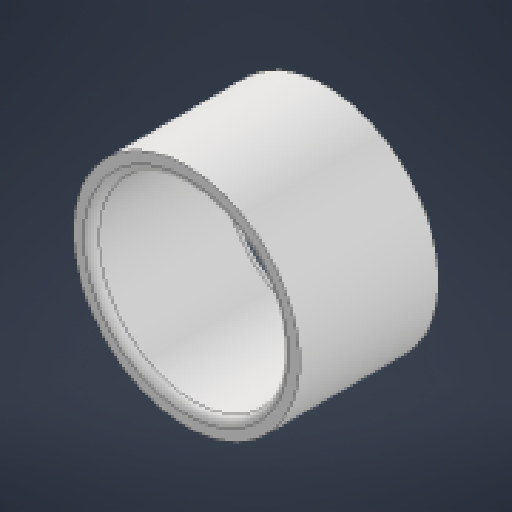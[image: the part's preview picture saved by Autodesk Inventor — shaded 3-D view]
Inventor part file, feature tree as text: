
AUTODESK INVENTOR PART (.ipt)
format: ipt  version: 2024.1 (Build 281209000, 209)  size: 156,160 bytes
history: native  units: in
note: dims shown in document units (in); Inventor stores cm internally (conversion verified against a paired STEP export)
features: other x4, reference x2, extrude x1, fillet x1, sketch x1
ambient origin geometry x8: Origin, YZ Plane, XZ Plane, XY Plane, X Axis, Y Axis, Z Axis, Center Point
bodies: Solid1 (feature_tree)
feature tree (9):
  extrude  "Extrusion1"  Depth=0.005in
  fillet  "Fillet1"  Radius=0.0925in
  sketch  "Sketch1"  dims[d0=0.003in d1=0.005in d2=0.0925in d3=0.0in d4=0.005in]
  reference  "Reference1"
  reference  "Reference2"
  other  "<userpath>\Documents\School\FallCAD\Bio\Bio.iam"
  other  "Bio.iam"
  other  "ServoMount:1"
  other  "FrontLinkage:1"
